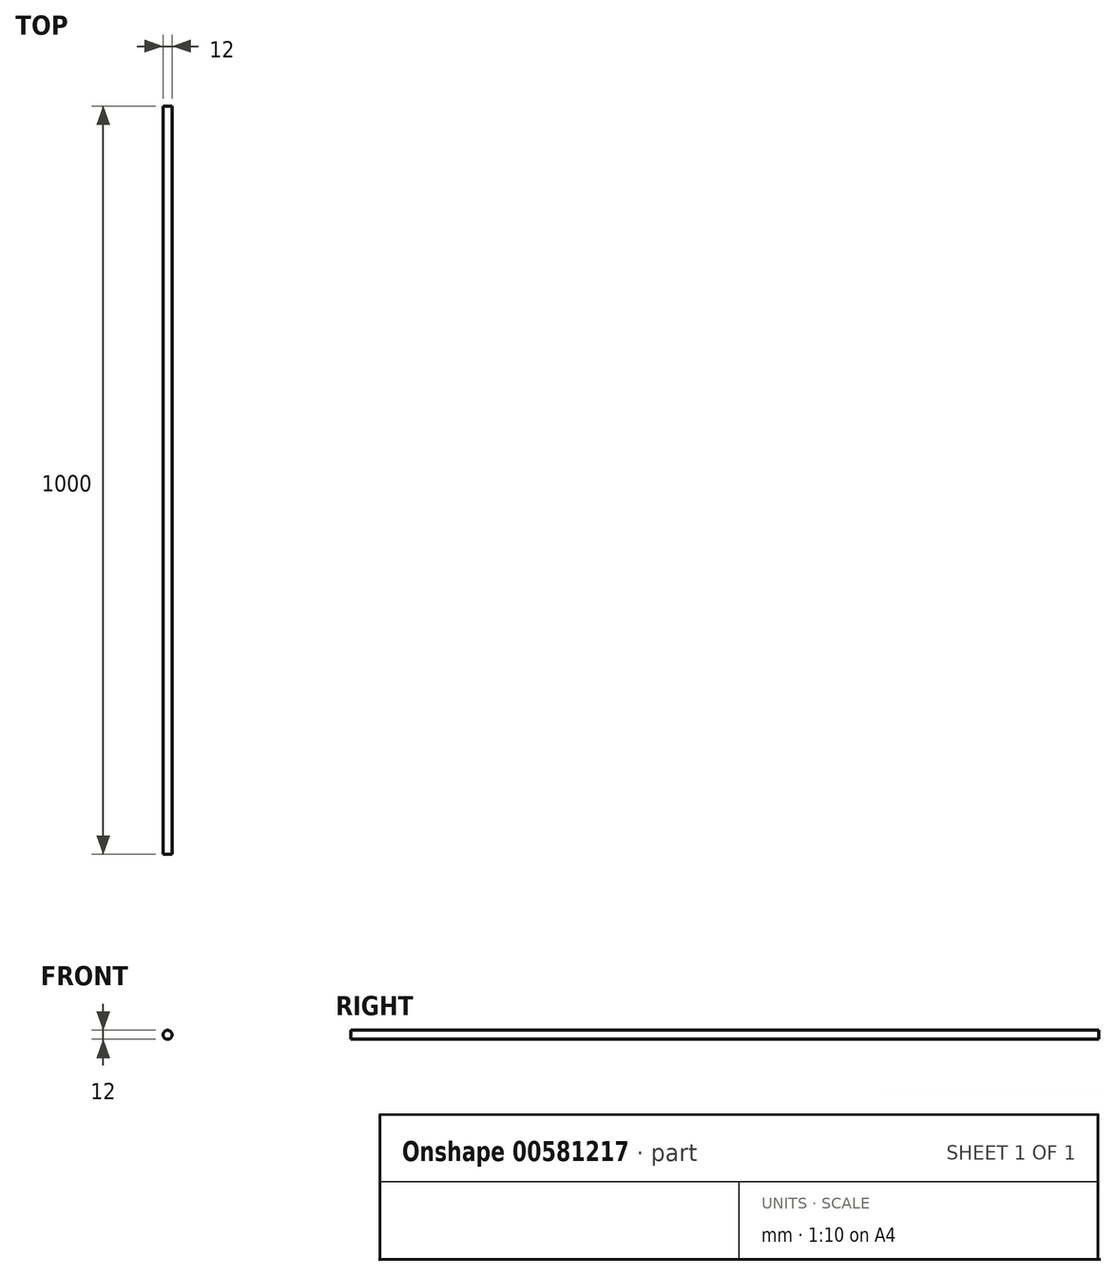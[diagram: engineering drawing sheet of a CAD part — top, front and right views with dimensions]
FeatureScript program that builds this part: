
annotation { "Feature Type Name" : "Feature", "Feature Type Description" : "" }
export const myFeature = defineFeature(function(context is Context, id is Id, definition is map)
    precondition{}
    {
        {
            var Q0;
            Q0=qCreatedBy(makeId("Front.planeOp"),FACE);
            var sketch = newSketch(context, id + "F0", { "sketchPlane" : qUnion([Q0])});
            skCircle(sketch, "E0", {"center": v(0, 0) * mm, "radius": 6 * mm});
            skSolve(sketch);
        }
        {
            var Q0;
            Q0 = qSketchRegion(id + "F0", true);
            extrude(context, id + "F1", {"entities" : qUnion([Q0]), "depth" : 1000 * mm, "offsetDistance" : 25.4 * mm});
        }
    });
